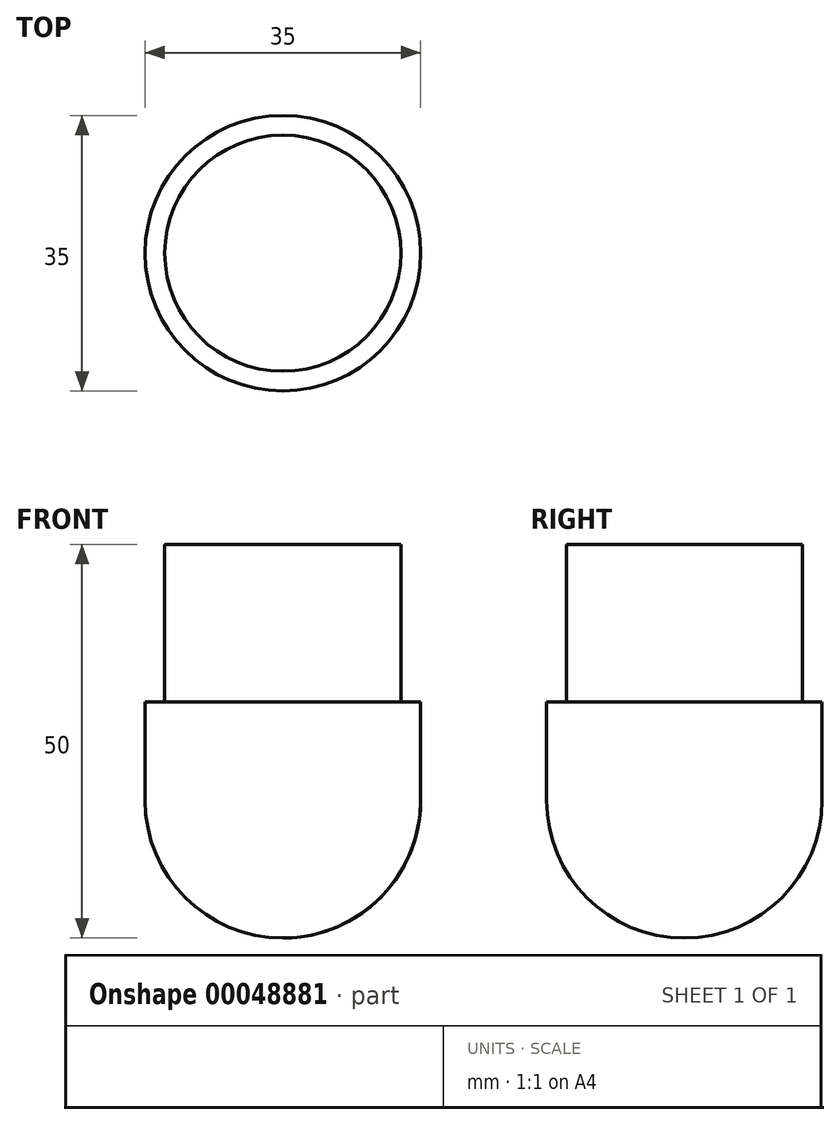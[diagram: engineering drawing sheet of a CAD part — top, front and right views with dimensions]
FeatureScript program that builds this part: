
annotation { "Feature Type Name" : "Feature", "Feature Type Description" : "" }
export const myFeature = defineFeature(function(context is Context, id is Id, definition is map)
    precondition{}
    {
        {
            var Q0;
            Q0=qCreatedBy(makeId("Top.planeOp"),FACE);
            var sketch = newSketch(context, id + "F0", { "sketchPlane" : qUnion([Q0])});
            skCircle(sketch, "E0", {"center": v(-56.12, 20.1) * mm, "radius": 15 * mm});
            skCircle(sketch, "E1", {"center": v(-56.12, 20.1) * mm, "radius": 17.5 * mm});
            skSolve(sketch);
        }
        {
            var Q0;
            Q0=makeQuery(id+"F0.imprint","IMPRINT",FACE,{"disambiguationData":[TD([[makeQuery(id+"F0.imprint","IMPRINT",EDGE,{"derivedFrom":sQuery(id+"F0.wireOp",EDGE,"E0")}),1.0]])]});
            extrude(context, id + "F1", {"entities" : qUnion([Q0]), "depth" : 20 * mm});
        }
        {
            var Q0;
            Q0=makeQuery(id+"F0.imprint","IMPRINT",FACE,{"disambiguationData":[TD([[makeQuery(id+"F0.imprint","IMPRINT",EDGE,{"derivedFrom":sQuery(id+"F0.wireOp",EDGE,"E0")}),-1.0]])]});
            var Q1;
            Q1=makeQuery(id+"F0.imprint","IMPRINT",FACE,{"disambiguationData":[TD([[makeQuery(id+"F0.imprint","IMPRINT",EDGE,{"derivedFrom":sQuery(id+"F0.wireOp",EDGE,"E0")}),1.0]])]});
            extrude(context, id + "F2", {"entities" : qUnion([Q0, Q1]), "operationType" : NewBodyOperationType.ADD, "oppositeDirection" : true, "depth" : 30 * mm});
        }
        {
            var Q0;
            Q0=makeQuery(id+"F2.opExtrude","CAP_EDGE",EDGE,{"disambiguationData":[OSD([sQuery(id+"F0.wireOp",EDGE,"E1")])],"isStart":false});
            fillet(context, id + "F3", {"entities" : qUnion([Q0]), "radius" : 17.5 * mm, "tangentPropagation" : true, "allowEdgeOverflow" : false});
        }
    });
